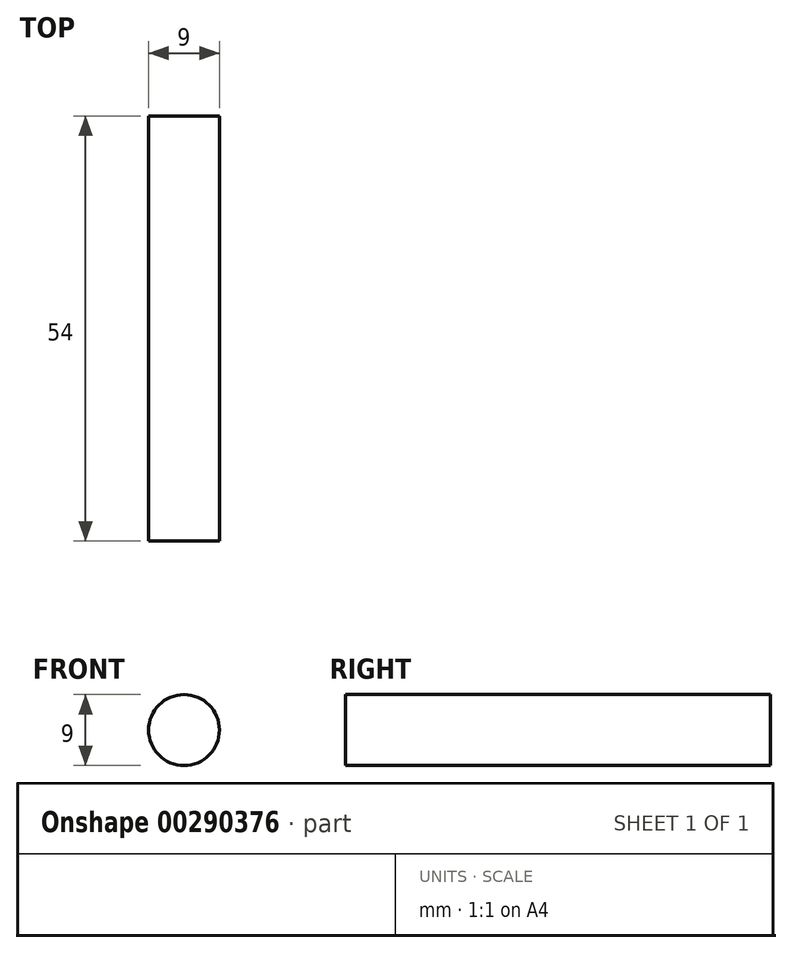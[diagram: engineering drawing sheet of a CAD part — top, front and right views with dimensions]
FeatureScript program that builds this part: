
annotation { "Feature Type Name" : "Feature", "Feature Type Description" : "" }
export const myFeature = defineFeature(function(context is Context, id is Id, definition is map)
    precondition{}
    {
        {
            var Q0;
            Q0=qCreatedBy(makeId("Front.planeOp"),FACE);
            var sketch = newSketch(context, id + "F0", { "sketchPlane" : qUnion([Q0])});
            skCircle(sketch, "E0", {"center": v(0, 0) * mm, "radius": 4.5 * mm});
            skSolve(sketch);
        }
        {
            var Q0;
            Q0=makeQuery(id+"F0.imprint","IMPRINT",FACE,{"disambiguationData":[TD([[makeQuery(id+"F0.imprint","IMPRINT",EDGE,{"derivedFrom":sQuery(id+"F0.wireOp",EDGE,"E0")}),1.0]])]});
            extrude(context, id + "F1", {"entities" : qUnion([Q0]), "endBound" : BoundingType.SYMMETRIC, "depth" : 54 * mm});
        }
    });
